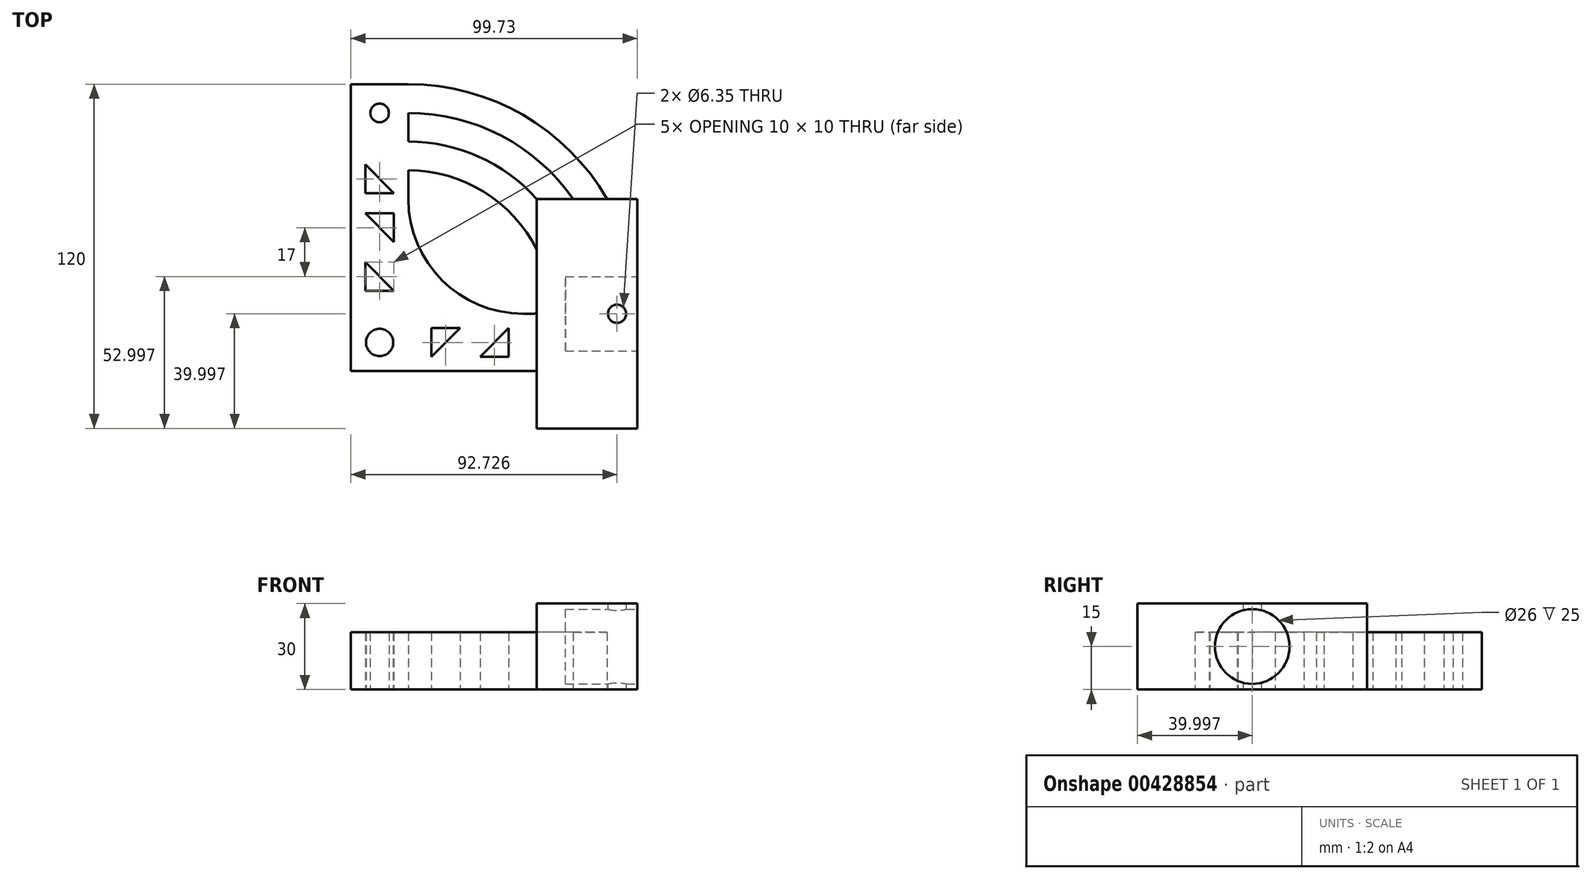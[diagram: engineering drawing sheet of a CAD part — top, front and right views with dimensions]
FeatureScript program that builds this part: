
annotation { "Feature Type Name" : "Feature", "Feature Type Description" : "" }
export const myFeature = defineFeature(function(context is Context, id is Id, definition is map)
    precondition{}
    {
        {
            var Q0;
            Q0=qCreatedBy(makeId("Top.planeOp"),FACE);
            var sketch = newSketch(context, id + "F0", { "sketchPlane" : qUnion([Q0])});
            skLineSegment(sketch, "E0.bottom", {"start": v(-3.1, 70.2) * mm, "end": v(-23.1, 70.2) * mm});
            skLineSegment(sketch, "E0.top", {"start": v(-3.1, -29.8) * mm, "end": v(-23.1, -29.8) * mm});
            skLineSegment(sketch, "E0.left", {"start": v(-3.1, 70.2) * mm, "end": v(-3.1, 30.2) * mm});
            skLineSegment(sketch, "E0.right", {"start": v(-23.1, 70.2) * mm, "end": v(-23.1, -29.8) * mm});
            skLineSegment(sketch, "E1.bottom", {"start": v(36.9, -9.8) * mm, "end": v(40.62, -9.8) * mm});
            skLineSegment(sketch, "E1.top", {"start": v(-3.1, -29.8) * mm, "end": v(40.62, -29.8) * mm});
            skLineSegment(sketch, "E1.left", {"start": v(-3.1, -9.8) * mm, "end": v(-3.1, -29.8) * mm});
            skCircle(sketch, "E2", {"center": v(-13.1, -19.8) * mm, "radius": 4.75 * mm});
            skLineSegment(sketch, "E3", {"start": v(-8.1, 15.2) * mm, "end": v(-18.1, 25.2) * mm});
            skLineSegment(sketch, "E4", {"start": v(-18.1, 25.2) * mm, "end": v(-8.1, 25.2) * mm});
            skLineSegment(sketch, "E5", {"start": v(-8.1, 25.2) * mm, "end": v(-8.1, 15.2) * mm});
            skLineSegment(sketch, "E6", {"start": v(-18.1, 8.2) * mm, "end": v(-8.1, -1.8) * mm});
            skLineSegment(sketch, "E7", {"start": v(-8.1, -1.8) * mm, "end": v(-18.1, -1.8) * mm});
            skLineSegment(sketch, "E8", {"start": v(-18.1, -1.8) * mm, "end": v(-18.1, 8.2) * mm});
            skCircle(sketch, "E9", {"center": v(-13.1, 60.2) * mm, "radius": 3.25 * mm});
            skLineSegment(sketch, "E10", {"start": v(-18.1, 42.2) * mm, "end": v(-8.1, 32.2) * mm});
            skLineSegment(sketch, "E11", {"start": v(-8.1, 32.2) * mm, "end": v(-18.1, 32.2) * mm});
            skLineSegment(sketch, "E12", {"start": v(-18.1, 32.2) * mm, "end": v(-18.1, 42.2) * mm});
            skLineSegment(sketch, "E13", {"start": v(21.9, -24.8) * mm, "end": v(31.9, -14.8) * mm});
            skLineSegment(sketch, "E14", {"start": v(31.9, -14.8) * mm, "end": v(31.9, -24.8) * mm});
            skLineSegment(sketch, "E15", {"start": v(31.9, -24.8) * mm, "end": v(21.9, -24.8) * mm});
            skLineSegment(sketch, "E16", {"start": v(14.9, -14.8) * mm, "end": v(4.9, -24.8) * mm});
            skLineSegment(sketch, "E17", {"start": v(4.9, -24.8) * mm, "end": v(4.9, -14.8) * mm});
            skLineSegment(sketch, "E18", {"start": v(4.9, -14.8) * mm, "end": v(14.9, -14.8) * mm});
            skCircle(sketch, "E19", {"center": v(-3.1, -9.8) * mm, "radius": 80 * mm});
            skCircle(sketch, "E20", {"center": v(-3.1, -9.8) * mm, "radius": 70 * mm});
            skCircle(sketch, "E21", {"center": v(-3.1, -9.8) * mm, "radius": 60 * mm});
            skCircle(sketch, "E22", {"center": v(-3.1, -9.8) * mm, "radius": 50 * mm});
            skLineSegment(sketch, "E23.bottom", {"start": v(76.62, -49.8) * mm, "end": v(41.62, -49.8) * mm});
            skLineSegment(sketch, "E23.top", {"start": v(76.62, 30.2) * mm, "end": v(41.62, 30.2) * mm});
            skLineSegment(sketch, "E23.left", {"start": v(76.62, -49.8) * mm, "end": v(76.62, 30.2) * mm});
            skLineSegment(sketch, "E23.right", {"start": v(41.62, -8.8) * mm, "end": v(41.62, 30.2) * mm});
            skPoint(sketch, "E24", {"position": v(41.62, -9.8) * mm});
            skArc(sketch, "E25.filletArc", {"start": v(40.62, -9.8) * mm, "mid": v(41.32, -9.51) * mm, "end": v(41.62, -8.8) * mm});
            skLineSegment(sketch, "E26", {"start": v(41.62, -30.8) * mm, "end": v(41.62, -49.8) * mm});
            skLineSegment(sketch, "E27", {"start": v(41.62, -8.8) * mm, "end": v(41.62, -30.8) * mm});
            skArc(sketch, "E28.filletArc", {"start": v(-3.1, 30.2) * mm, "mid": v(8.61, 1.91) * mm, "end": v(36.9, -9.8) * mm});
            skLineSegment(sketch, "E29", {"start": v(40.62, -29.8) * mm, "end": v(41.62, -29.8) * mm});
            skCircle(sketch, "E30", {"center": v(69.62, -9.8) * mm, "radius": 3.18 * mm});
            skSolve(sketch);
        }
        {
            var Q0;
            {var subQ0=sQuery(id+"F0.wireOp",EDGE,"E23.top");var subQ1=sQuery(id+"F0.wireOp",EDGE,"E19");var subQ2=makeQuery(id+"F0.imprint","INTERSECT",VERTEX,{"derivedFrom":[subQ1,subQ0]});Q0=makeQuery(id+"F0.imprint","IMPRINT",FACE,{"disambiguationData":[TD([[makeQuery(id+"F0.imprint","IMPRINT",EDGE,{"disambiguationData":[TD([[subQ2,1.0]])],"derivedFrom":subQ1}),-1.0]])]});}
            var Q1;
            {var subQ0=sQuery(id+"F0.wireOp",EDGE,"E23.top");var subQ8=sQuery(id+"F0.wireOp",EDGE,"E19");var subQ9=makeQuery(id+"F0.imprint","INTERSECT",VERTEX,{"derivedFrom":[subQ8,subQ0]});Q1=makeQuery(id+"F0.imprint","IMPRINT",FACE,{"disambiguationData":[TD([[makeQuery(id+"F0.imprint","IMPRINT",EDGE,{"disambiguationData":[TD([[subQ9,1.0]])],"derivedFrom":subQ8}),1.0]])]});}
            var Q2;
            {var subQ0=sQuery(id+"F0.wireOp",EDGE,"E23.bottom");var subQ5=sQuery(id+"F0.wireOp",EDGE,"E20");var subQ9=makeQuery(id+"F0.imprint","INTERSECT",VERTEX,{"derivedFrom":[subQ5,subQ0]});Q2=makeQuery(id+"F0.imprint","IMPRINT",FACE,{"disambiguationData":[TD([[makeQuery(id+"F0.imprint","IMPRINT",EDGE,{"disambiguationData":[TD([[subQ9,-1.0]])],"derivedFrom":subQ5}),1.0]])]});}
            var Q3;
            {var subQ0=sQuery(id+"F0.wireOp",EDGE,"E23.bottom");var subQ1=sQuery(id+"F0.wireOp",EDGE,"E19");var subQ2=makeQuery(id+"F0.imprint","INTERSECT",VERTEX,{"derivedFrom":[subQ1,subQ0]});Q3=makeQuery(id+"F0.imprint","IMPRINT",FACE,{"disambiguationData":[TD([[makeQuery(id+"F0.imprint","IMPRINT",EDGE,{"disambiguationData":[TD([[subQ2,-1.0]])],"derivedFrom":subQ1}),-1.0]])]});}
            var Q4;
            {var subQ3=sQuery(id+"F0.wireOp",EDGE,"E23.right");var subQ5=sQuery(id+"F0.wireOp",EDGE,"E22");var subQ7=makeQuery(id+"F0.imprint","INTERSECT",VERTEX,{"derivedFrom":[subQ5,subQ3]});Q4=makeQuery(id+"F0.imprint","IMPRINT",FACE,{"disambiguationData":[TD([[makeQuery(id+"F0.imprint","IMPRINT",EDGE,{"disambiguationData":[TD([[subQ7,1.0]])],"derivedFrom":subQ5}),-1.0]])]});}
            var Q5;
            {var subQ3=sQuery(id+"F0.wireOp",EDGE,"E22");var subQ5=sQuery(id+"F0.wireOp",EDGE,"E23.right");var subQ8=makeQuery(id+"F0.imprint","INTERSECT",VERTEX,{"derivedFrom":[subQ3,subQ5]});Q5=makeQuery(id+"F0.imprint","IMPRINT",FACE,{"disambiguationData":[TD([[makeQuery(id+"F0.imprint","IMPRINT",EDGE,{"disambiguationData":[TD([[subQ8,1.0]])],"derivedFrom":subQ3}),1.0]])]});}
            var Q6;
            {var subQ11=sQuery(id+"F0.wireOp",EDGE,"E0.top");Q6=makeQuery(id+"F0.imprint","IMPRINT",FACE,{"disambiguationData":[TD([[makeQuery(id+"F0.imprint","IMPRINT",EDGE,{"derivedFrom":subQ11}),-1.0]])]});}
            var Q7;
            {var subQ5=sQuery(id+"F0.wireOp",EDGE,"E21");var subQ6=sQuery(id+"F0.wireOp",EDGE,"E0.left");var subQ7=makeQuery(id+"F0.imprint","INTERSECT",VERTEX,{"derivedFrom":[subQ6,subQ5]});Q7=makeQuery(id+"F0.imprint","IMPRINT",FACE,{"disambiguationData":[TD([[makeQuery(id+"F0.imprint","IMPRINT",EDGE,{"disambiguationData":[TD([[subQ7,-1.0]])],"derivedFrom":subQ6}),-1.0]])]});}
            var Q8;
            {var subQ0=sQuery(id+"F0.wireOp",EDGE,"E20");var subQ1=sQuery(id+"F0.wireOp",EDGE,"E0.left");var subQ2=makeQuery(id+"F0.imprint","INTERSECT",VERTEX,{"derivedFrom":[subQ1,subQ0]});Q8=makeQuery(id+"F0.imprint","IMPRINT",FACE,{"disambiguationData":[TD([[makeQuery(id+"F0.imprint","IMPRINT",EDGE,{"disambiguationData":[TD([[subQ2,-1.0]])],"derivedFrom":subQ1}),-1.0]])]});}
            var Q9;
            {var subQ0=sQuery(id+"F0.wireOp",EDGE,"E19");var subQ3=sQuery(id+"F0.wireOp",EDGE,"E0.right");var subQ4=makeQuery(id+"F0.imprint","INTERSECT",VERTEX,{"derivedFrom":[subQ3,subQ0]});Q9=makeQuery(id+"F0.imprint","IMPRINT",FACE,{"disambiguationData":[TD([[makeQuery(id+"F0.imprint","IMPRINT",EDGE,{"disambiguationData":[TD([[subQ4,-1.0]])],"derivedFrom":subQ3}),1.0]])]});}
            var Q10;
            {var subQ0=sQuery(id+"F0.wireOp",EDGE,"E0.bottom");Q10=makeQuery(id+"F0.imprint","IMPRINT",FACE,{"disambiguationData":[TD([[makeQuery(id+"F0.imprint","IMPRINT",EDGE,{"derivedFrom":subQ0}),1.0]])]});}
            var Q11;
            {var subQ1=sQuery(id+"F0.wireOp",EDGE,"E0.left");var subQ3=sQuery(id+"F0.wireOp",EDGE,"E20");var subQ4=makeQuery(id+"F0.imprint","INTERSECT",VERTEX,{"derivedFrom":[subQ1,subQ3]});Q11=makeQuery(id+"F0.imprint","IMPRINT",FACE,{"disambiguationData":[TD([[makeQuery(id+"F0.imprint","IMPRINT",EDGE,{"disambiguationData":[TD([[subQ4,1.0]])],"derivedFrom":subQ3}),-1.0]])]});}
            var Q12;
            {var subQ0=sQuery(id+"F0.wireOp",EDGE,"E21");var subQ1=sQuery(id+"F0.wireOp",EDGE,"E0.left");var subQ2=makeQuery(id+"F0.imprint","INTERSECT",VERTEX,{"derivedFrom":[subQ1,subQ0]});Q12=makeQuery(id+"F0.imprint","IMPRINT",FACE,{"disambiguationData":[TD([[makeQuery(id+"F0.imprint","IMPRINT",EDGE,{"disambiguationData":[TD([[subQ2,-1.0]])],"derivedFrom":subQ1}),1.0]])]});}
            extrude(context, id + "F1", {"entities" : qUnion([Q0, Q1, Q2, Q3, Q4, Q5, Q6, Q7, Q8, Q9, Q10, Q11, Q12]), "depth" : 20 * mm});
        }
        {
            var Q0;
            {var subQ3=sQuery(id+"F0.wireOp",EDGE,"E23.right");var subQ5=sQuery(id+"F0.wireOp",EDGE,"E22");var subQ7=makeQuery(id+"F0.imprint","INTERSECT",VERTEX,{"derivedFrom":[subQ5,subQ3]});Q0=makeQuery(id+"F0.imprint","IMPRINT",FACE,{"disambiguationData":[TD([[makeQuery(id+"F0.imprint","IMPRINT",EDGE,{"disambiguationData":[TD([[subQ7,1.0]])],"derivedFrom":subQ5}),-1.0]])]});}
            var Q1;
            {var subQ0=sQuery(id+"F0.wireOp",EDGE,"E23.bottom");var subQ5=sQuery(id+"F0.wireOp",EDGE,"E20");var subQ9=makeQuery(id+"F0.imprint","INTERSECT",VERTEX,{"derivedFrom":[subQ5,subQ0]});Q1=makeQuery(id+"F0.imprint","IMPRINT",FACE,{"disambiguationData":[TD([[makeQuery(id+"F0.imprint","IMPRINT",EDGE,{"disambiguationData":[TD([[subQ9,-1.0]])],"derivedFrom":subQ5}),1.0]])]});}
            var Q2;
            {var subQ0=sQuery(id+"F0.wireOp",EDGE,"E23.top");var subQ8=sQuery(id+"F0.wireOp",EDGE,"E19");var subQ9=makeQuery(id+"F0.imprint","INTERSECT",VERTEX,{"derivedFrom":[subQ8,subQ0]});Q2=makeQuery(id+"F0.imprint","IMPRINT",FACE,{"disambiguationData":[TD([[makeQuery(id+"F0.imprint","IMPRINT",EDGE,{"disambiguationData":[TD([[subQ9,1.0]])],"derivedFrom":subQ8}),1.0]])]});}
            var Q3;
            {var subQ0=sQuery(id+"F0.wireOp",EDGE,"E23.bottom");var subQ1=sQuery(id+"F0.wireOp",EDGE,"E19");var subQ2=makeQuery(id+"F0.imprint","INTERSECT",VERTEX,{"derivedFrom":[subQ1,subQ0]});Q3=makeQuery(id+"F0.imprint","IMPRINT",FACE,{"disambiguationData":[TD([[makeQuery(id+"F0.imprint","IMPRINT",EDGE,{"disambiguationData":[TD([[subQ2,-1.0]])],"derivedFrom":subQ1}),-1.0]])]});}
            var Q4;
            {var subQ0=sQuery(id+"F0.wireOp",EDGE,"E23.top");var subQ1=sQuery(id+"F0.wireOp",EDGE,"E19");var subQ2=makeQuery(id+"F0.imprint","INTERSECT",VERTEX,{"derivedFrom":[subQ1,subQ0]});Q4=makeQuery(id+"F0.imprint","IMPRINT",FACE,{"disambiguationData":[TD([[makeQuery(id+"F0.imprint","IMPRINT",EDGE,{"disambiguationData":[TD([[subQ2,1.0]])],"derivedFrom":subQ1}),-1.0]])]});}
            var Q5;
            {var subQ3=sQuery(id+"F0.wireOp",EDGE,"E22");var subQ5=sQuery(id+"F0.wireOp",EDGE,"E23.right");var subQ8=makeQuery(id+"F0.imprint","INTERSECT",VERTEX,{"derivedFrom":[subQ3,subQ5]});Q5=makeQuery(id+"F0.imprint","IMPRINT",FACE,{"disambiguationData":[TD([[makeQuery(id+"F0.imprint","IMPRINT",EDGE,{"disambiguationData":[TD([[subQ8,1.0]])],"derivedFrom":subQ3}),1.0]])]});}
            extrude(context, id + "F2", {"entities" : qUnion([Q0, Q1, Q2, Q3, Q4, Q5]), "operationType" : NewBodyOperationType.ADD, "depth" : 30 * mm});
        }
        {
            var Q0;
            {var subQ0=sQuery(id+"F0.wireOp",EDGE,"E23.left");Q0=makeQuery(id+"F2.boolean.opBoolean","MERGE",FACE,{"derivedFrom":[makeQuery(id+"F1.opExtrude","SWEPT_FACE",FACE,{"disambiguationData":[OSD([subQ0])]}),makeQuery(id+"F2.opExtrude","SWEPT_FACE",FACE,{"disambiguationData":[OSD([subQ0])]})]});}
            var sketch = newSketch(context, id + "F3", { "sketchPlane" : qUnion([Q0])});
            skCircle(sketch, "E31", {"center": v(-9.8, 15) * mm, "radius": 13 * mm});
            skSolve(sketch);
        }
        {
            var Q0;
            Q0 = qSketchRegion(id + "F3", true);
            extrude(context, id + "F4", {"entities" : qUnion([Q0]), "operationType" : NewBodyOperationType.REMOVE, "oppositeDirection" : true, "depth" : 25 * mm});
        }
    });
